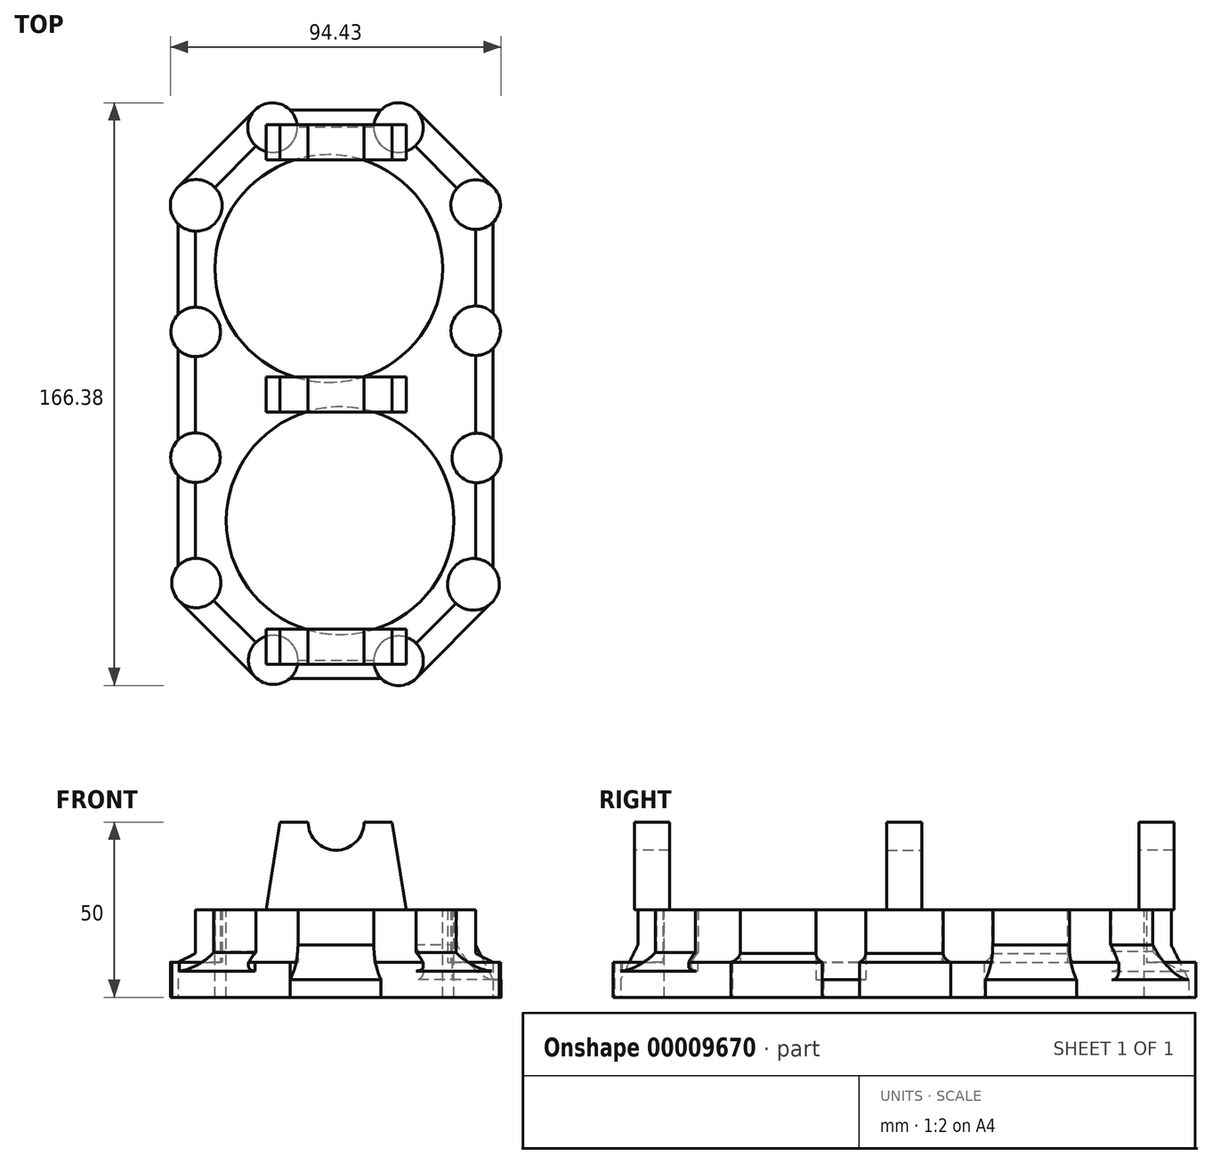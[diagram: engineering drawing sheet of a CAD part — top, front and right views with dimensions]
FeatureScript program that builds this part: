
annotation { "Feature Type Name" : "Feature", "Feature Type Description" : "" }
export const myFeature = defineFeature(function(context is Context, id is Id, definition is map)
    precondition{}
    {
        {
            var Q0;
            Q0=qCreatedBy(makeId("Top.planeOp"),FACE);
            var sketch = newSketch(context, id + "F0", { "sketchPlane" : qUnion([Q0])});
            skArc(sketch, "E0", {"start": v(-19.18, -25.03) * mm, "mid": v(-16.91, -19.71) * mm, "end": v(-19.18, -14.4) * mm});
            skArc(sketch, "E1", {"start": v(-19.58, -61.03) * mm, "mid": v(-17.43, -56.11) * mm, "end": v(-19.18, -51.03) * mm});
            skArc(sketch, "E2", {"start": v(-87.17, -82.21) * mm, "mid": v(-82.25, -84.37) * mm, "end": v(-77.18, -82.63) * mm});
            skArc(sketch, "E3", {"start": v(-109.18, -50.63) * mm, "mid": v(-110.92, -55.7) * mm, "end": v(-108.76, -60.62) * mm});
            skLineSegment(sketch, "E4", {"start": v(-87.17, -82.21) * mm, "end": v(-108.76, -60.62) * mm});
            skLineSegment(sketch, "E5", {"start": v(-109.18, -50.63) * mm, "end": v(-109.18, -24.63) * mm});
            skLineSegment(sketch, "E6", {"start": v(-109.18, -14.63) * mm, "end": v(-109.18, 11.37) * mm});
            skLineSegment(sketch, "E7", {"start": v(-19.18, 11.6) * mm, "end": v(-19.18, -14.4) * mm});
            skLineSegment(sketch, "E8", {"start": v(-19.18, -25.03) * mm, "end": v(-19.18, -51.03) * mm});
            skLineSegment(sketch, "E9", {"start": v(-77.18, -82.63) * mm, "end": v(-51.18, -82.63) * mm});
            skLineSegment(sketch, "E10", {"start": v(-109.18, 21.17) * mm, "end": v(-109.18, 47.17) * mm});
            skArc(sketch, "E11", {"start": v(-109.18, 57.6) * mm, "mid": v(-111.34, 52.39) * mm, "end": v(-109.18, 47.17) * mm});
            skLineSegment(sketch, "E12", {"start": v(-109.18, 57.6) * mm, "end": v(-87.18, 79.6) * mm});
            skArc(sketch, "E13", {"start": v(-77.18, 79.6) * mm, "mid": v(-82.18, 81.68) * mm, "end": v(-87.18, 79.6) * mm});
            skLineSegment(sketch, "E14", {"start": v(-51.18, 79.6) * mm, "end": v(-77.18, 79.6) * mm});
            skLineSegment(sketch, "E15", {"start": v(-19.58, -61.03) * mm, "end": v(-41.18, -82.63) * mm});
            skArc(sketch, "E16", {"start": v(-51.18, -82.63) * mm, "mid": v(-46.18, -84.7) * mm, "end": v(-41.18, -82.63) * mm});
            skArc(sketch, "E17", {"start": v(-109.18, -14.63) * mm, "mid": v(-111.25, -19.63) * mm, "end": v(-109.18, -24.63) * mm});
            skArc(sketch, "E18", {"start": v(-19.18, 11.6) * mm, "mid": v(-17.1, 16.6) * mm, "end": v(-19.18, 21.6) * mm});
            skArc(sketch, "E19", {"start": v(-109.18, 21.17) * mm, "mid": v(-111.15, 16.27) * mm, "end": v(-109.18, 11.37) * mm});
            skLineSegment(sketch, "E20", {"start": v(-19.18, 21.6) * mm, "end": v(-19.18, 47.6) * mm});
            skArc(sketch, "E21", {"start": v(-19.18, 47.6) * mm, "mid": v(-17.1, 52.6) * mm, "end": v(-19.18, 57.6) * mm});
            skArc(sketch, "E22", {"start": v(-41.18, 79.6) * mm, "mid": v(-46.18, 81.68) * mm, "end": v(-51.18, 79.6) * mm});
            skLineSegment(sketch, "E23", {"start": v(-19.18, 57.6) * mm, "end": v(-41.18, 79.6) * mm});
            skLineSegment(sketch, "E24", {"start": v(-19.18, -1.63) * mm, "end": v(-109.18, -1.63) * mm, "construction": true});
            skSolve(sketch);
        }
        {
            var Q0;
            Q0=makeQuery(id+"F0.imprint","IMPRINT",FACE,{"disambiguationData":[TD([[makeQuery(id+"F0.imprint","IMPRINT",EDGE,{"derivedFrom":sQuery(id+"F0.wireOp",EDGE,"E0")}),1.0]])]});
            extrude(context, id + "F1", {"entities" : qUnion([Q0]), "depth" : 5 * mm});
        }
        {
            var Q0;
            Q0=makeQuery(id+"F1.opExtrude","CAP_FACE",FACE,{"disambiguationData":[OSD([sQuery(id+"F0.wireOp",EDGE,"E0"),sQuery(id+"F0.wireOp",EDGE,"E1"),sQuery(id+"F0.wireOp",EDGE,"E2"),sQuery(id+"F0.wireOp",EDGE,"E3"),sQuery(id+"F0.wireOp",EDGE,"E4"),sQuery(id+"F0.wireOp",EDGE,"E5"),sQuery(id+"F0.wireOp",EDGE,"E6"),sQuery(id+"F0.wireOp",EDGE,"E7"),sQuery(id+"F0.wireOp",EDGE,"E8"),sQuery(id+"F0.wireOp",EDGE,"E9"),sQuery(id+"F0.wireOp",EDGE,"E10"),sQuery(id+"F0.wireOp",EDGE,"E11"),sQuery(id+"F0.wireOp",EDGE,"E12"),sQuery(id+"F0.wireOp",EDGE,"E13"),sQuery(id+"F0.wireOp",EDGE,"E14"),sQuery(id+"F0.wireOp",EDGE,"E15"),sQuery(id+"F0.wireOp",EDGE,"E16"),sQuery(id+"F0.wireOp",EDGE,"E17"),sQuery(id+"F0.wireOp",EDGE,"E18"),sQuery(id+"F0.wireOp",EDGE,"E19"),sQuery(id+"F0.wireOp",EDGE,"E20"),sQuery(id+"F0.wireOp",EDGE,"E21"),sQuery(id+"F0.wireOp",EDGE,"E22"),sQuery(id+"F0.wireOp",EDGE,"E23")])],"isStart":false});
            var sketch = newSketch(context, id + "F2", { "sketchPlane" : qUnion([Q0])});
            skArc(sketch, "E25", {"start": v(-109.18, -24.63) * mm, "mid": v(-97.1, -19.63) * mm, "end": v(-109.18, -14.63) * mm});
            skArc(sketch, "E26", {"start": v(-109.18, 11.37) * mm, "mid": v(-97, 16.27) * mm, "end": v(-109.18, 21.17) * mm});
            skArc(sketch, "E27", {"start": v(-108.76, -60.62) * mm, "mid": v(-96.9, -55.13) * mm, "end": v(-109.18, -50.63) * mm});
            skArc(sketch, "E28", {"start": v(-77.18, -82.63) * mm, "mid": v(-81.67, -70.36) * mm, "end": v(-87.17, -82.21) * mm});
            skArc(sketch, "E29", {"start": v(-41.18, -82.63) * mm, "mid": v(-46.18, -70.56) * mm, "end": v(-51.18, -82.63) * mm});
            skArc(sketch, "E30", {"start": v(-19.18, -51.03) * mm, "mid": v(-32.18, -55.51) * mm, "end": v(-19.58, -61.03) * mm});
            skArc(sketch, "E31", {"start": v(-19.18, -14.4) * mm, "mid": v(-30.9, -19.71) * mm, "end": v(-19.18, -25.03) * mm});
            skArc(sketch, "E32", {"start": v(-19.18, 21.6) * mm, "mid": v(-31.25, 16.6) * mm, "end": v(-19.18, 11.6) * mm});
            skArc(sketch, "E33", {"start": v(-19.18, 57.6) * mm, "mid": v(-31.25, 52.6) * mm, "end": v(-19.18, 47.6) * mm});
            skArc(sketch, "E34", {"start": v(-51.18, 79.6) * mm, "mid": v(-46.18, 67.54) * mm, "end": v(-41.18, 79.6) * mm});
            skArc(sketch, "E35", {"start": v(-87.18, 79.6) * mm, "mid": v(-82.18, 67.54) * mm, "end": v(-77.18, 79.6) * mm});
            skArc(sketch, "E36", {"start": v(-109.18, 47.17) * mm, "mid": v(-96.57, 52.39) * mm, "end": v(-109.18, 57.6) * mm});
            skSolve(sketch);
        }
        {
            var Q0;
            Q0=sQuery(id+"F0.wireOp",EDGE,"E24");
            cPlane(context, id + "F3", {"entities" : qUnion([Q0]), "cplaneType" : CPlaneType.LINE_ANGLE, "offset" : 150 * mm, "angle" : 0 * degree, "width" : 150 * mm, "height" : 150 * mm});
        }
        {
            var Q0;
            Q0=qCreatedBy(id+"F3.planeOp",FACE);
            cPlane(context, id + "F4", {"entities" : qUnion([Q0]), "cplaneType" : CPlaneType.OFFSET, "offset" : 36 * mm, "width" : 150 * mm, "height" : 150 * mm});
        }
        {
            var Q0;
            Q0=qCreatedBy(id+"F3.planeOp",FACE);
            cPlane(context, id + "F5", {"entities" : qUnion([Q0]), "cplaneType" : CPlaneType.OFFSET, "offset" : 36 * mm, "oppositeDirection" : true, "width" : 150 * mm, "height" : 150 * mm});
        }
        {
            var Q0;
            Q0=makeQuery(id+"F2.imprint","IMPRINT",FACE,{"disambiguationData":[TD([[makeQuery(id+"F2.imprint","IMPRINT",EDGE,{"derivedFrom":sQuery(id+"F2.wireOp",EDGE,"E25")}),-1.0]])]});
            extrude(context, id + "F6", {"entities" : qUnion([Q0]), "depth" : 10 * mm});
        }
        {
            var Q0;
            Q0=makeQuery(id+"F6.opExtrude","CAP_FACE",FACE,{"disambiguationData":[OSD([sQuery(id+"F0.wireOp",EDGE,"E4"),sQuery(id+"F0.wireOp",EDGE,"E5"),sQuery(id+"F0.wireOp",EDGE,"E6"),sQuery(id+"F0.wireOp",EDGE,"E7"),sQuery(id+"F0.wireOp",EDGE,"E8"),sQuery(id+"F0.wireOp",EDGE,"E9"),sQuery(id+"F0.wireOp",EDGE,"E10"),sQuery(id+"F0.wireOp",EDGE,"E12"),sQuery(id+"F0.wireOp",EDGE,"E14"),sQuery(id+"F0.wireOp",EDGE,"E15"),sQuery(id+"F0.wireOp",EDGE,"E20"),sQuery(id+"F0.wireOp",EDGE,"E23"),sQuery(id+"F2.wireOp",EDGE,"E25"),sQuery(id+"F2.wireOp",EDGE,"E26"),sQuery(id+"F2.wireOp",EDGE,"E27"),sQuery(id+"F2.wireOp",EDGE,"E28"),sQuery(id+"F2.wireOp",EDGE,"E29"),sQuery(id+"F2.wireOp",EDGE,"E30"),sQuery(id+"F2.wireOp",EDGE,"E31"),sQuery(id+"F2.wireOp",EDGE,"E32"),sQuery(id+"F2.wireOp",EDGE,"E33"),sQuery(id+"F2.wireOp",EDGE,"E34"),sQuery(id+"F2.wireOp",EDGE,"E35"),sQuery(id+"F2.wireOp",EDGE,"E36")])],"isStart":false});
            var sketch = newSketch(context, id + "F7", { "sketchPlane" : qUnion([Q0])});
            skCircle(sketch, "E37", {"center": v(-66.13, 34.37) * mm, "radius": 32.5 * mm});
            skCircle(sketch, "E38", {"center": v(-62.86, -37.63) * mm, "radius": 32.5 * mm});
            skSolve(sketch);
        }
        {
            var Q0;
            Q0=makeQuery(id+"F7.imprint","IMPRINT",FACE,{"disambiguationData":[TD([[makeQuery(id+"F7.imprint","IMPRINT",EDGE,{"derivedFrom":sQuery(id+"F7.wireOp",EDGE,"E37")}),1.0]])]});
            var Q1;
            Q1=makeQuery(id+"F7.imprint","IMPRINT",FACE,{"disambiguationData":[TD([[makeQuery(id+"F7.imprint","IMPRINT",EDGE,{"derivedFrom":sQuery(id+"F7.wireOp",EDGE,"E38")}),1.0]])]});
            extrude(context, id + "F8", {"entities" : qUnion([Q0, Q1]), "operationType" : NewBodyOperationType.REMOVE, "oppositeDirection" : true, "depth" : 40 * mm});
        }
        {
            var Q0;
            Q0=makeQuery(id+"F6.opExtrude","CAP_FACE",FACE,{"disambiguationData":[OSD([sQuery(id+"F0.wireOp",EDGE,"E4"),sQuery(id+"F0.wireOp",EDGE,"E5"),sQuery(id+"F0.wireOp",EDGE,"E6"),sQuery(id+"F0.wireOp",EDGE,"E7"),sQuery(id+"F0.wireOp",EDGE,"E8"),sQuery(id+"F0.wireOp",EDGE,"E9"),sQuery(id+"F0.wireOp",EDGE,"E10"),sQuery(id+"F0.wireOp",EDGE,"E12"),sQuery(id+"F0.wireOp",EDGE,"E14"),sQuery(id+"F0.wireOp",EDGE,"E15"),sQuery(id+"F0.wireOp",EDGE,"E20"),sQuery(id+"F0.wireOp",EDGE,"E23"),sQuery(id+"F2.wireOp",EDGE,"E25"),sQuery(id+"F2.wireOp",EDGE,"E26"),sQuery(id+"F2.wireOp",EDGE,"E27"),sQuery(id+"F2.wireOp",EDGE,"E28"),sQuery(id+"F2.wireOp",EDGE,"E29"),sQuery(id+"F2.wireOp",EDGE,"E30"),sQuery(id+"F2.wireOp",EDGE,"E31"),sQuery(id+"F2.wireOp",EDGE,"E32"),sQuery(id+"F2.wireOp",EDGE,"E33"),sQuery(id+"F2.wireOp",EDGE,"E34"),sQuery(id+"F2.wireOp",EDGE,"E35"),sQuery(id+"F2.wireOp",EDGE,"E36")])],"isStart":false});
            var sketch = newSketch(context, id + "F9", { "sketchPlane" : qUnion([Q0])});
            skLineSegment(sketch, "E39", {"start": v(-24.18, 9.54) * mm, "end": v(-24.18, -12.65) * mm});
            skLineSegment(sketch, "E40", {"start": v(-104.18, 9.2) * mm, "end": v(-104.18, -12.56) * mm});
            skLineSegment(sketch, "E41", {"start": v(-24.18, 23.68) * mm, "end": v(-24.18, 45.54) * mm});
            skLineSegment(sketch, "E42", {"start": v(-24.18, -26.78) * mm, "end": v(-24.18, -48.46) * mm});
            skLineSegment(sketch, "E43", {"start": v(-104.18, 45) * mm, "end": v(-104.18, 23.34) * mm});
            skLineSegment(sketch, "E44", {"start": v(-104.18, -26.7) * mm, "end": v(-104.18, -48.35) * mm});
            skLineSegment(sketch, "E45", {"start": v(-29.47, 57.3) * mm, "end": v(-41.49, 69.31) * mm});
            skLineSegment(sketch, "E46", {"start": v(-53.25, 74.6) * mm, "end": v(-75.1, 74.6) * mm});
            skLineSegment(sketch, "E47", {"start": v(-86.86, 69.31) * mm, "end": v(-98.65, 57.52) * mm});
            skLineSegment(sketch, "E48", {"start": v(-98.97, -60.42) * mm, "end": v(-86.97, -72.43) * mm});
            skLineSegment(sketch, "E49", {"start": v(-53.25, -77.63) * mm, "end": v(-74.9, -77.63) * mm});
            skLineSegment(sketch, "E50", {"start": v(-29.8, -61.25) * mm, "end": v(-41.18, -72.63) * mm});
            skSolve(sketch);
        }
        {
            var Q0;
            {var subQ7=sQuery(id+"F9.wireOp",EDGE,"E39");Q0=makeQuery(id+"F9.imprint","IMPRINT",FACE,{"disambiguationData":[TD([[makeQuery(id+"F9.imprint","IMPRINT",EDGE,{"derivedFrom":subQ7}),-1.0]])]});}
            extrude(context, id + "F10", {"entities" : qUnion([Q0]), "operationType" : NewBodyOperationType.ADD, "depth" : 10 * mm});
        }
        {
            var Q0;
            Q0=makeQuery(id+"F6.opExtrude","CAP_EDGE",EDGE,{"disambiguationData":[OSD([sQuery(id+"F0.wireOp",EDGE,"E6")])],"isStart":false});
            var Q1;
            Q1=makeQuery(id+"F6.opExtrude","CAP_EDGE",EDGE,{"disambiguationData":[OSD([sQuery(id+"F0.wireOp",EDGE,"E10")])],"isStart":false});
            var Q2;
            Q2=makeQuery(id+"F6.opExtrude","CAP_EDGE",EDGE,{"disambiguationData":[OSD([sQuery(id+"F0.wireOp",EDGE,"E5")])],"isStart":false});
            var Q3;
            Q3=makeQuery(id+"F6.opExtrude","CAP_EDGE",EDGE,{"disambiguationData":[OSD([sQuery(id+"F0.wireOp",EDGE,"E8")])],"isStart":false});
            var Q4;
            Q4=makeQuery(id+"F6.opExtrude","CAP_EDGE",EDGE,{"disambiguationData":[OSD([sQuery(id+"F0.wireOp",EDGE,"E7")])],"isStart":false});
            chamfer(context, id + "F11", {"entities" : qUnion([Q0, Q1, Q2, Q3, Q4]), "chamferType" : ChamferType.TWO_OFFSETS, "width1" : 10 * mm, "oppositeDirection" : false, "width2" : 5 * mm, "tangentPropagation" : true});
        }
        {
            var Q0;
            Q0=makeQuery(id+"F6.opExtrude","CAP_EDGE",EDGE,{"disambiguationData":[OSD([sQuery(id+"F0.wireOp",EDGE,"E12")])],"isStart":false});
            var Q1;
            Q1=makeQuery(id+"F6.opExtrude","CAP_EDGE",EDGE,{"disambiguationData":[OSD([sQuery(id+"F0.wireOp",EDGE,"E15")])],"isStart":false});
            var Q2;
            Q2=makeQuery(id+"F6.opExtrude","CAP_EDGE",EDGE,{"disambiguationData":[OSD([sQuery(id+"F0.wireOp",EDGE,"E4")])],"isStart":false});
            chamfer(context, id + "F12", {"entities" : qUnion([Q0, Q1, Q2]), "chamferType" : ChamferType.TWO_OFFSETS, "width1" : 10 * mm, "oppositeDirection" : false, "width2" : 7.5 * mm, "tangentPropagation" : true});
        }
        {
            var Q0;
            Q0=makeQuery(id+"F6.opExtrude","CAP_EDGE",EDGE,{"disambiguationData":[OSD([sQuery(id+"F0.wireOp",EDGE,"E20")])],"isStart":false});
            var Q1;
            Q1=makeQuery(id+"F6.opExtrude","CAP_EDGE",EDGE,{"disambiguationData":[OSD([sQuery(id+"F0.wireOp",EDGE,"E14")])],"isStart":false});
            var Q2;
            Q2=makeQuery(id+"F6.opExtrude","CAP_EDGE",EDGE,{"disambiguationData":[OSD([sQuery(id+"F0.wireOp",EDGE,"E9")])],"isStart":false});
            chamfer(context, id + "F13", {"entities" : qUnion([Q0, Q1, Q2]), "chamferType" : ChamferType.TWO_OFFSETS, "width1" : 5 * mm, "oppositeDirection" : false, "width2" : 10 * mm, "tangentPropagation" : true});
        }
        {
            var Q0;
            Q0=makeQuery(id+"F6.opExtrude","CAP_EDGE",EDGE,{"disambiguationData":[OSD([sQuery(id+"F0.wireOp",EDGE,"E23")])],"isStart":false});
            chamfer(context, id + "F14", {"entities" : qUnion([Q0]), "chamferType" : ChamferType.TWO_OFFSETS, "width1" : 7.5 * mm, "oppositeDirection" : false, "width2" : 10 * mm, "tangentPropagation" : true});
        }
        {
            var Q0;
            Q0=makeQuery(id+"F2.imprint","IMPRINT",FACE,{"disambiguationData":[TD([[makeQuery(id+"F2.imprint","IMPRINT",EDGE,{"derivedFrom":sQuery(id+"F2.wireOp",EDGE,"E30")}),1.0]])]});
            var Q1;
            Q1=makeQuery(id+"F2.imprint","IMPRINT",FACE,{"disambiguationData":[TD([[makeQuery(id+"F2.imprint","IMPRINT",EDGE,{"derivedFrom":sQuery(id+"F2.wireOp",EDGE,"E29")}),1.0]])]});
            var Q2;
            Q2=makeQuery(id+"F2.imprint","IMPRINT",FACE,{"disambiguationData":[TD([[makeQuery(id+"F2.imprint","IMPRINT",EDGE,{"derivedFrom":sQuery(id+"F2.wireOp",EDGE,"E28")}),1.0]])]});
            var Q3;
            Q3=makeQuery(id+"F2.imprint","IMPRINT",FACE,{"disambiguationData":[TD([[makeQuery(id+"F2.imprint","IMPRINT",EDGE,{"derivedFrom":sQuery(id+"F2.wireOp",EDGE,"E27")}),1.0]])]});
            var Q4;
            Q4=makeQuery(id+"F2.imprint","IMPRINT",FACE,{"disambiguationData":[TD([[makeQuery(id+"F2.imprint","IMPRINT",EDGE,{"derivedFrom":sQuery(id+"F2.wireOp",EDGE,"E25")}),1.0]])]});
            var Q5;
            Q5=makeQuery(id+"F2.imprint","IMPRINT",FACE,{"disambiguationData":[TD([[makeQuery(id+"F2.imprint","IMPRINT",EDGE,{"derivedFrom":sQuery(id+"F2.wireOp",EDGE,"E26")}),1.0]])]});
            var Q6;
            Q6=makeQuery(id+"F2.imprint","IMPRINT",FACE,{"disambiguationData":[TD([[makeQuery(id+"F2.imprint","IMPRINT",EDGE,{"derivedFrom":sQuery(id+"F2.wireOp",EDGE,"E32")}),1.0]])]});
            var Q7;
            Q7=makeQuery(id+"F2.imprint","IMPRINT",FACE,{"disambiguationData":[TD([[makeQuery(id+"F2.imprint","IMPRINT",EDGE,{"derivedFrom":sQuery(id+"F2.wireOp",EDGE,"E33")}),1.0]])]});
            var Q8;
            Q8=makeQuery(id+"F2.imprint","IMPRINT",FACE,{"disambiguationData":[TD([[makeQuery(id+"F2.imprint","IMPRINT",EDGE,{"derivedFrom":sQuery(id+"F2.wireOp",EDGE,"E34")}),1.0]])]});
            var Q9;
            Q9=makeQuery(id+"F2.imprint","IMPRINT",FACE,{"disambiguationData":[TD([[makeQuery(id+"F2.imprint","IMPRINT",EDGE,{"derivedFrom":sQuery(id+"F2.wireOp",EDGE,"E36")}),1.0]])]});
            var Q10;
            Q10=makeQuery(id+"F2.imprint","IMPRINT",FACE,{"disambiguationData":[TD([[makeQuery(id+"F2.imprint","IMPRINT",EDGE,{"derivedFrom":sQuery(id+"F2.wireOp",EDGE,"E35")}),1.0]])]});
            extrude(context, id + "F15", {"entities" : qUnion([Q0, Q1, Q2, Q3, Q4, Q5, Q6, Q7, Q8, Q9, Q10]), "operationType" : NewBodyOperationType.ADD, "depth" : 5 * mm});
        }
        {
            var Q0;
            Q0=qCreatedBy(id+"F3.planeOp",FACE);
            var sketch = newSketch(context, id + "F16", { "sketchPlane" : qUnion([Q0])});
            skLineSegment(sketch, "E51", {"start": v(-44.02, 25) * mm, "end": v(-48.02, 50) * mm});
            skLineSegment(sketch, "E52", {"start": v(-80.02, 50) * mm, "end": v(-84.02, 25) * mm});
            skLineSegment(sketch, "E53", {"start": v(-84.02, 25) * mm, "end": v(-44.02, 25) * mm});
            skArc(sketch, "E54", {"start": v(-72.02, 50) * mm, "mid": v(-64.02, 42) * mm, "end": v(-56.02, 50) * mm});
            skLineSegment(sketch, "E55", {"start": v(-48.02, 50) * mm, "end": v(-56.02, 50) * mm});
            skLineSegment(sketch, "E56", {"start": v(-72.02, 50) * mm, "end": v(-80.02, 50) * mm});
            skSolve(sketch);
        }
        {
            var Q0;
            Q0=makeQuery(id+"F16.imprint","IMPRINT",FACE,{"disambiguationData":[TD([[makeQuery(id+"F16.imprint","IMPRINT",EDGE,{"derivedFrom":sQuery(id+"F16.wireOp",EDGE,"E51")}),1.0]])]});
            extrude(context, id + "F17", {"entities" : qUnion([Q0]), "depth" : 10 * mm, "symmetric" : true});
        }
        {
            var Q0;
            Q0=makeQuery(id+"F17.opExtrude","SWEPT_BODY",BODY,{"disambiguationData":[OSD([sQuery(id+"F16.wireOp",EDGE,"E51"),sQuery(id+"F16.wireOp",EDGE,"E52"),sQuery(id+"F16.wireOp",EDGE,"E53"),sQuery(id+"F16.wireOp",EDGE,"E54"),sQuery(id+"F16.wireOp",EDGE,"E55"),sQuery(id+"F16.wireOp",EDGE,"E56")])]});
            var Q1;
            Q1=qCreatedBy(id+"F5.planeOp",FACE);
            mirror(context, id + "F18", {"entities" : qUnion([Q0]), "mirrorPlane" : qUnion([Q1])});
        }
        {
            var Q0;
            Q0=makeQuery(id+"F17.opExtrude","SWEPT_BODY",BODY,{"disambiguationData":[OSD([sQuery(id+"F16.wireOp",EDGE,"E51"),sQuery(id+"F16.wireOp",EDGE,"E52"),sQuery(id+"F16.wireOp",EDGE,"E53"),sQuery(id+"F16.wireOp",EDGE,"E54"),sQuery(id+"F16.wireOp",EDGE,"E55"),sQuery(id+"F16.wireOp",EDGE,"E56")])]});
            var Q1;
            Q1=qCreatedBy(id+"F4.planeOp",FACE);
            mirror(context, id + "F19", {"entities" : qUnion([Q0]), "mirrorPlane" : qUnion([Q1])});
        }
    });
